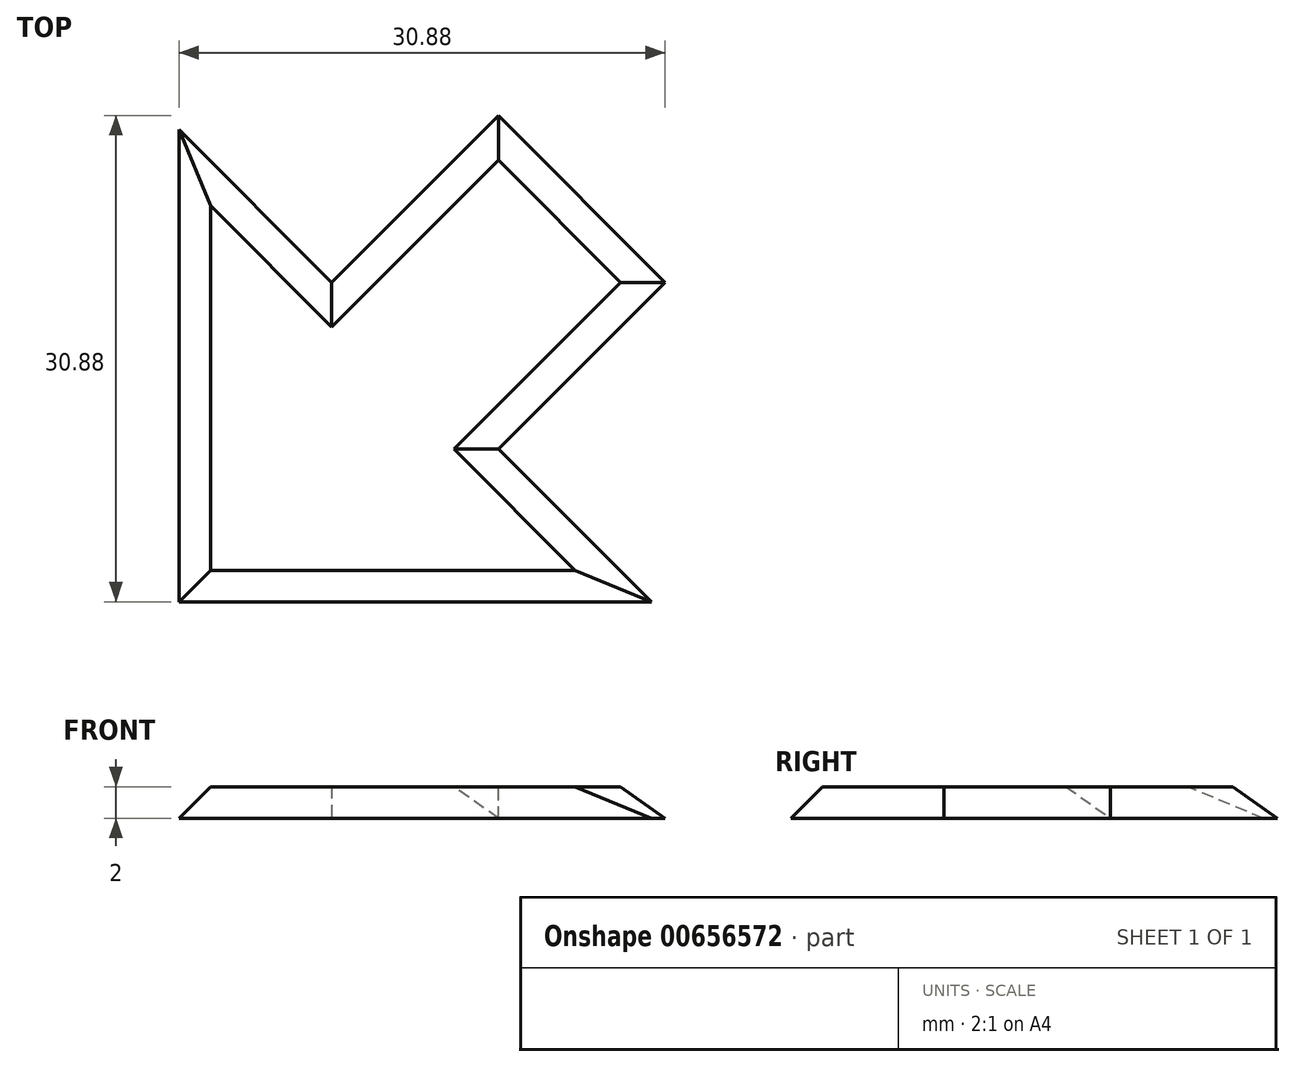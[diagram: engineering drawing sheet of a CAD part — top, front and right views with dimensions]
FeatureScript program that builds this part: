
annotation { "Feature Type Name" : "Feature", "Feature Type Description" : "" }
export const myFeature = defineFeature(function(context is Context, id is Id, definition is map)
    precondition{}
    {
        {
            var Q0;
            Q0=qCreatedBy(makeId("Top.planeOp"),FACE);
            var sketch = newSketch(context, id + "F0", { "sketchPlane" : qUnion([Q0])});
            skLineSegment(sketch, "E0", {"start": v(0, 0) * mm, "end": v(0, 30) * mm});
            skLineSegment(sketch, "E1", {"start": v(0, 30) * mm, "end": v(9.7, 20.3) * mm});
            skLineSegment(sketch, "E2", {"start": v(9.7, 20.3) * mm, "end": v(20.3, 30.88) * mm});
            skLineSegment(sketch, "E3", {"start": v(20.3, 30.88) * mm, "end": v(30.88, 20.3) * mm});
            skLineSegment(sketch, "E4", {"start": v(30.88, 20.3) * mm, "end": v(20.3, 9.7) * mm});
            skLineSegment(sketch, "E5", {"start": v(20.3, 9.7) * mm, "end": v(30, 0) * mm});
            skLineSegment(sketch, "E6", {"start": v(30, 0) * mm, "end": v(0, 0) * mm});
            skSolve(sketch);
        }
        {
            var Q0;
            Q0 = qSketchRegion(id + "F0", true);
            extrude(context, id + "F1", {"entities" : qUnion([Q0]), "depth" : 2 * mm, "offsetDistance" : 25 * mm});
        }
        {
            var Q0;
            Q0=makeQuery(id+"F1.opExtrude","CAP_EDGE",EDGE,{"disambiguationData":[OSD([sQuery(id+"F0.wireOp",EDGE,"E4")])],"isStart":false});
            var Q1;
            Q1=makeQuery(id+"F1.opExtrude","CAP_EDGE",EDGE,{"disambiguationData":[OSD([sQuery(id+"F0.wireOp",EDGE,"E2")])],"isStart":false});
            var Q2;
            Q2=makeQuery(id+"F1.opExtrude","CAP_EDGE",EDGE,{"disambiguationData":[OSD([sQuery(id+"F0.wireOp",EDGE,"E5")])],"isStart":false});
            var Q3;
            Q3=makeQuery(id+"F1.opExtrude","CAP_EDGE",EDGE,{"disambiguationData":[OSD([sQuery(id+"F0.wireOp",EDGE,"E6")])],"isStart":false});
            var Q4;
            Q4=makeQuery(id+"F1.opExtrude","CAP_EDGE",EDGE,{"disambiguationData":[OSD([sQuery(id+"F0.wireOp",EDGE,"E0")])],"isStart":false});
            var Q5;
            Q5=makeQuery(id+"F1.opExtrude","CAP_EDGE",EDGE,{"disambiguationData":[OSD([sQuery(id+"F0.wireOp",EDGE,"E1")])],"isStart":false});
            var Q6;
            Q6=makeQuery(id+"F1.opExtrude","CAP_EDGE",EDGE,{"disambiguationData":[OSD([sQuery(id+"F0.wireOp",EDGE,"E3")])],"isStart":false});
            chamfer(context, id + "F2", {"entities" : qUnion([Q0, Q1, Q2, Q3, Q4, Q5, Q6]), "width" : 2 * mm, "tangentPropagation" : true});
        }
    });
